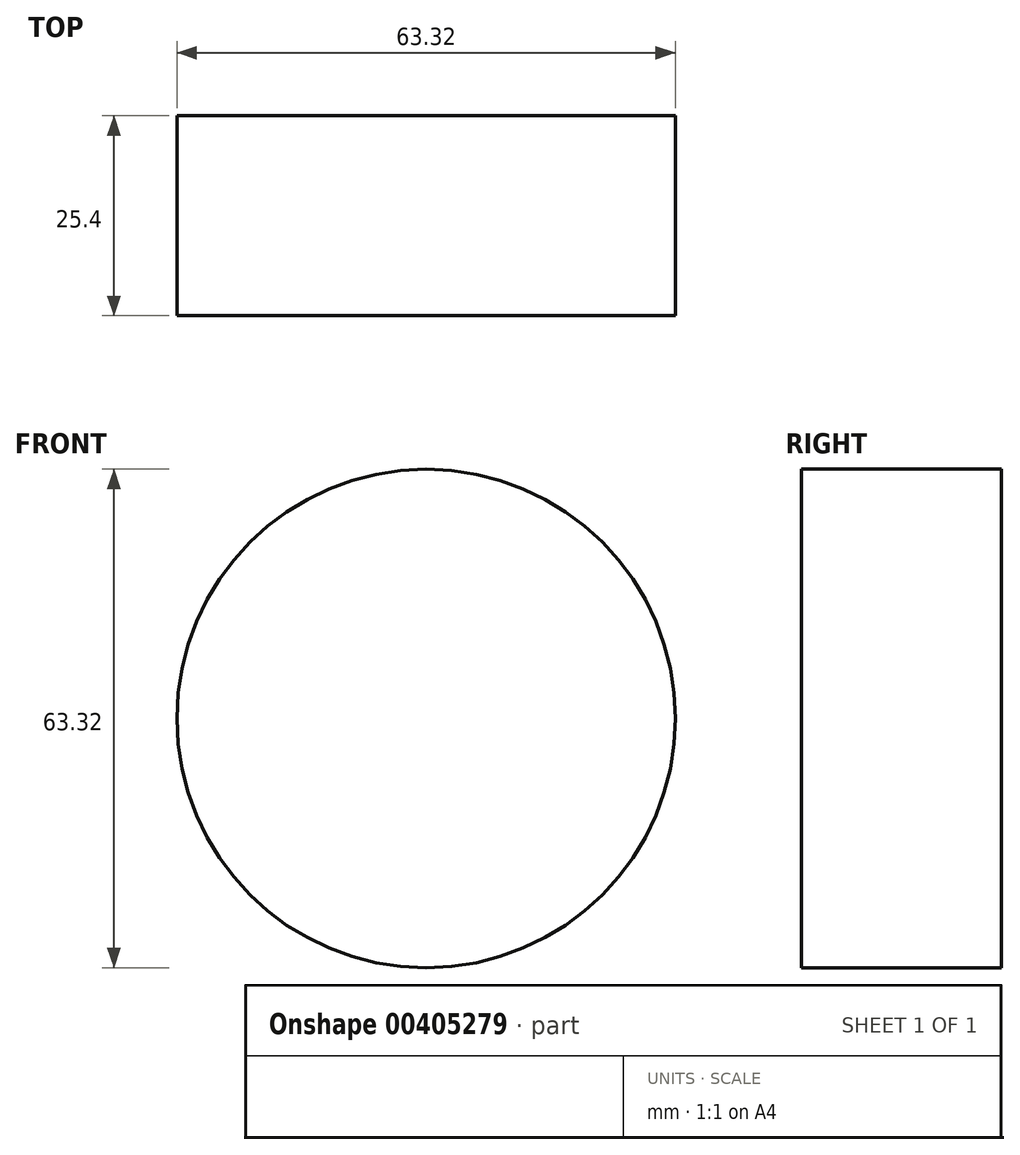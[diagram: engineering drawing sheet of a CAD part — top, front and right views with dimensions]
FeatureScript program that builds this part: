
annotation { "Feature Type Name" : "Feature", "Feature Type Description" : "" }
export const myFeature = defineFeature(function(context is Context, id is Id, definition is map)
    precondition{}
    {
        {
            var Q0;
            Q0=qCreatedBy(makeId("Front.planeOp"),FACE);
            var sketch = newSketch(context, id + "F0", { "sketchPlane" : qUnion([Q0])});
            skCircle(sketch, "E0", {"center": v(0, 0) * mm, "radius": 31.66 * mm});
            skSolve(sketch);
        }
        {
            var Q0;
            Q0=makeQuery(id+"F0.imprint","IMPRINT",FACE,{"disambiguationData":[TD([[makeQuery(id+"F0.imprint","IMPRINT",EDGE,{"derivedFrom":sQuery(id+"F0.wireOp",EDGE,"E0")}),1.0]])]});
            extrude(context, id + "F1", {"entities" : qUnion([Q0]), "depth" : 25.4 * mm});
        }
    });
